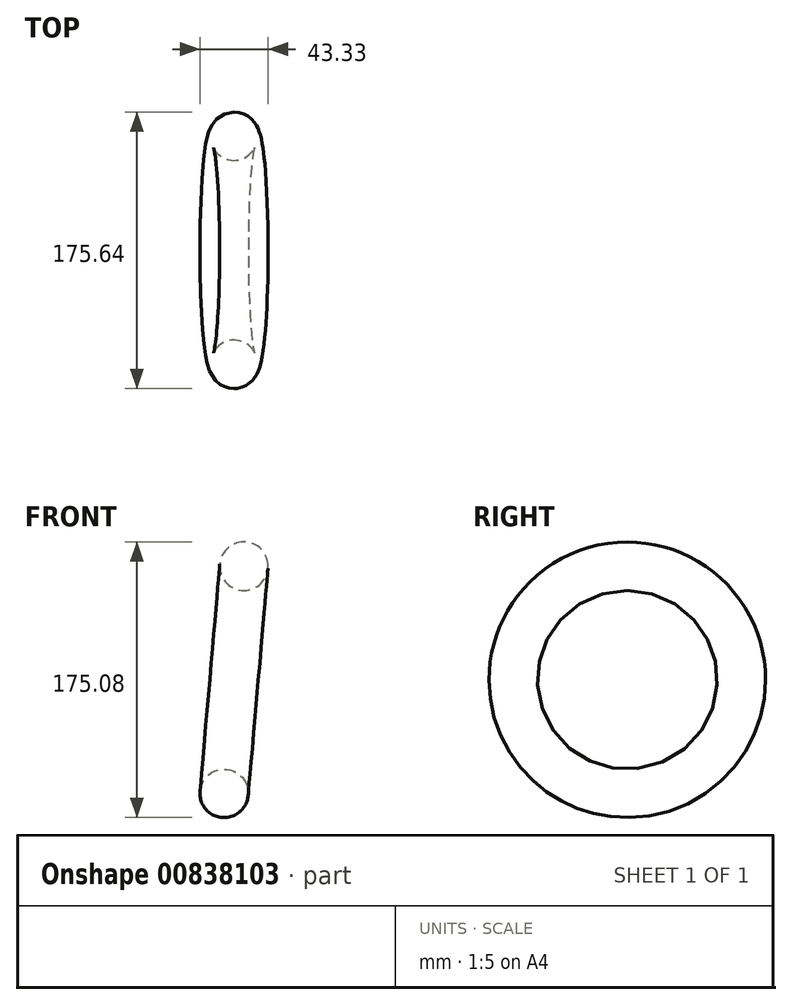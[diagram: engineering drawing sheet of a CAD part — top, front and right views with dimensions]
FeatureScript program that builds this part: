
annotation { "Feature Type Name" : "Feature", "Feature Type Description" : "" }
export const myFeature = defineFeature(function(context is Context, id is Id, definition is map)
    precondition{}
    {
        {
            var Q0;
            Q0=qCreatedBy(makeId("Front.planeOp"),FACE);
            var sketch = newSketch(context, id + "F0", { "sketchPlane" : qUnion([Q0])});
            skCircle(sketch, "E0", {"center": v(-20.66, 38.47) * mm, "radius": 5.34 * mm});
            skSolve(sketch);
        }
        {
            var Q0;
            Q0=sQuery(id+"F0.wireOp",EDGE,"E0");
            extrude(context, id + "F1", {"bodyType" : ToolBodyType.SURFACE, "surfaceEntities" : qUnion([Q0]), "depth" : 76.2 * mm, "offsetDistance" : 25.4 * mm});
        }
        {
            var Q0;
            Q0=qCreatedBy(makeId("Front.planeOp"),FACE);
            var sketch = newSketch(context, id + "F2", { "sketchPlane" : qUnion([Q0])});
            skCircle(sketch, "E1", {"center": v(-65.69, 39.25) * mm, "radius": 15.37 * mm});
            skLineSegment(sketch, "E2", {"start": v(18.3, -30.25) * mm, "end": v(-33.81, -36.25) * mm});
            skPoint(sketch, "E3", {"position": v(3.92, -36.25) * mm});
            skLineSegment(sketch, "E4", {"start": v(-33.81, -36.25) * mm, "end": v(18.97, -40.86) * mm});
            skSolve(sketch);
        }
        {
            var Q0;
            Q0 = qSketchRegion(id + "F2", true);
            var Q1;
            Q1=sQuery(id+"F2.wireOp",EDGE,"E4");
            revolve(context, id + "F3", {"surfaceOperationType" : NewSurfaceOperationType.NEW, "entities" : qUnion([Q0]), "axis" : qUnion([Q1]), "revolveType" : RevolveType.FULL});
        }
    });
